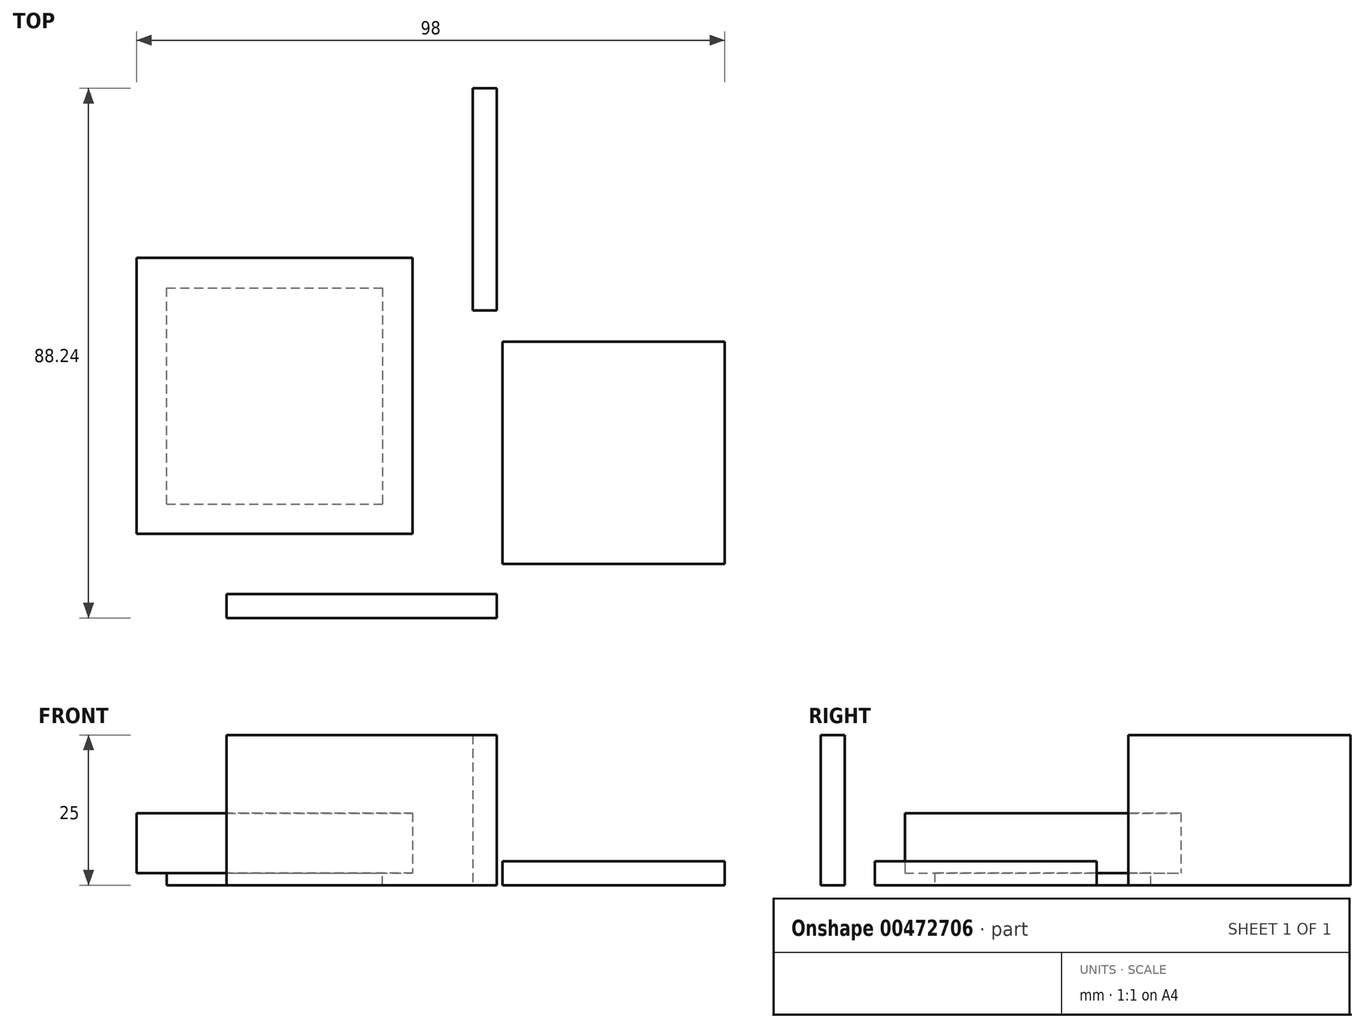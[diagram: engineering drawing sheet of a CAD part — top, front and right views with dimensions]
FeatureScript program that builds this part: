
annotation { "Feature Type Name" : "Feature", "Feature Type Description" : "" }
export const myFeature = defineFeature(function(context is Context, id is Id, definition is map)
    precondition{}
    {
        {
            var Q0;
            Q0=qCreatedBy(makeId("Top.planeOp"),FACE);
            var sketch = newSketch(context, id + "F0", { "sketchPlane" : qUnion([Q0])});
            skLineSegment(sketch, "E0", {"start": v(42, 5) * mm, "end": v(42, 42) * mm});
            skLineSegment(sketch, "E1", {"start": v(42, 42) * mm, "end": v(5, 42) * mm});
            skLineSegment(sketch, "E2", {"start": v(5, 42) * mm, "end": v(5, 5) * mm});
            skLineSegment(sketch, "E3", {"start": v(5, 5) * mm, "end": v(42, 5) * mm});
            skSolve(sketch);
        }
        {
            var Q0;
            Q0 = qSketchRegion(id + "F0", true);
            extrude(context, id + "F1", {"entities" : qUnion([Q0]), "depth" : 4 * mm});
        }
        {
            var Q0;
            Q0=qCreatedBy(makeId("Front.planeOp"),FACE);
            var sketch = newSketch(context, id + "F2", { "sketchPlane" : qUnion([Q0])});
            skLineSegment(sketch, "E4", {"start": v(0, 0) * mm, "end": v(4, 0) * mm});
            skLineSegment(sketch, "E5", {"start": v(4, 0) * mm, "end": v(4, 25) * mm});
            skLineSegment(sketch, "E6", {"start": v(4, 25) * mm, "end": v(-41, 25) * mm});
            skLineSegment(sketch, "E7", {"start": v(-41, 25) * mm, "end": v(-41, 0) * mm});
            skLineSegment(sketch, "E8", {"start": v(-41, 0) * mm, "end": v(0, 0) * mm});
            skSolve(sketch);
        }
        {
            var Q0;
            Q0 = qSketchRegion(id + "F2", true);
            extrude(context, id + "F3", {"entities" : qUnion([Q0]), "depth" : 4 * mm});
        }
        {
            var Q0;
            Q0=qCreatedBy(makeId("Right.planeOp"),FACE);
            var sketch = newSketch(context, id + "F4", { "sketchPlane" : qUnion([Q0])});
            skLineSegment(sketch, "E9", {"start": v(47.24, 0) * mm, "end": v(84.24, 0) * mm});
            skLineSegment(sketch, "E10", {"start": v(84.24, 0) * mm, "end": v(84.24, 25) * mm});
            skLineSegment(sketch, "E11", {"start": v(84.24, 25) * mm, "end": v(47.24, 25) * mm});
            skLineSegment(sketch, "E12", {"start": v(47.24, 25) * mm, "end": v(47.24, 0) * mm});
            skSolve(sketch);
        }
        {
            var Q0;
            Q0 = qSketchRegion(id + "F4", true);
            extrude(context, id + "F5", {"entities" : qUnion([Q0]), "depth" : 4 * mm});
        }
        {
            var Q0;
            Q0=qCreatedBy(makeId("Top.planeOp"),FACE);
            var sketch = newSketch(context, id + "F6", { "sketchPlane" : qUnion([Q0])});
            skLineSegment(sketch, "E13", {"start": v(0, 0) * mm, "end": v(0, 10) * mm, "construction": true});
            skLineSegment(sketch, "E14", {"start": v(0, 10) * mm, "end": v(-10, 10) * mm, "construction": true});
            skLineSegment(sketch, "E15", {"start": v(-10, 10) * mm, "end": v(-10, 56) * mm});
            skLineSegment(sketch, "E16", {"start": v(-10, 56) * mm, "end": v(-56, 56) * mm});
            skLineSegment(sketch, "E17", {"start": v(-56, 56) * mm, "end": v(-56, 10) * mm});
            skLineSegment(sketch, "E18", {"start": v(-56, 10) * mm, "end": v(-10, 10) * mm});
            skSolve(sketch);
        }
        {
            var Q0;
            Q0 = qSketchRegion(id + "F6", true);
            extrude(context, id + "F7", {"entities" : qUnion([Q0]), "depth" : 12 * mm});
        }
        {
            var Q0;
            Q0=qCreatedBy(makeId("Top.planeOp"),FACE);
            var sketch = newSketch(context, id + "F8", { "sketchPlane" : qUnion([Q0])});
            skLineSegment(sketch, "E19", {"start": v(0, 0) * mm, "end": v(0, 10) * mm, "construction": true});
            skLineSegment(sketch, "E20", {"start": v(0, 10) * mm, "end": v(-10, 10) * mm, "construction": true});
            skLineSegment(sketch, "E21", {"start": v(-10, 10) * mm, "end": v(-10, 56) * mm, "construction": true});
            skLineSegment(sketch, "E22", {"start": v(-10, 56) * mm, "end": v(-15, 56) * mm});
            skLineSegment(sketch, "E23", {"start": v(-15, 56) * mm, "end": v(-15, 15) * mm});
            skLineSegment(sketch, "E24", {"start": v(-15, 10) * mm, "end": v(-10, 10) * mm});
            skLineSegment(sketch, "E25", {"start": v(-10, 10) * mm, "end": v(-10, 56) * mm});
            skLineSegment(sketch, "E26", {"start": v(-10, 10) * mm, "end": v(-56, 10) * mm});
            skPoint(sketch, "E26.endSnap0", {"position": v(-12.5, 10) * mm});
            skLineSegment(sketch, "E27", {"start": v(-56, 10) * mm, "end": v(-56, 15) * mm});
            skLineSegment(sketch, "E28", {"start": v(-56, 15) * mm, "end": v(-15, 15) * mm});
            skSolve(sketch);
        }
        {
            var Q0;
            Q0 = qSketchRegion(id + "F8", true);
            extrude(context, id + "F9", {"entities" : qUnion([Q0]), "operationType" : NewBodyOperationType.REMOVE, "depth" : 2 * mm});
        }
        {
            var Q0;
            Q0=qCreatedBy(makeId("Top.planeOp"),FACE);
            var sketch = newSketch(context, id + "F10", { "sketchPlane" : qUnion([Q0])});
            skLineSegment(sketch, "E29", {"start": v(0, 0) * mm, "end": v(0, 10) * mm, "construction": true});
            skLineSegment(sketch, "E30", {"start": v(0, 10) * mm, "end": v(-10, 10) * mm, "construction": true});
            skLineSegment(sketch, "E31", {"start": v(-10, 10) * mm, "end": v(-10, 56) * mm, "construction": true});
            skLineSegment(sketch, "E32", {"start": v(-10, 56) * mm, "end": v(-56, 56) * mm});
            skLineSegment(sketch, "E33", {"start": v(-56, 56) * mm, "end": v(-56, 10) * mm});
            skLineSegment(sketch, "E34", {"start": v(-56, 10) * mm, "end": v(-51, 10) * mm});
            skLineSegment(sketch, "E35", {"start": v(-51, 10) * mm, "end": v(-51, 51) * mm});
            skLineSegment(sketch, "E36", {"start": v(-51, 51) * mm, "end": v(-10, 51) * mm});
            skLineSegment(sketch, "E37", {"start": v(-10, 51) * mm, "end": v(-10, 56) * mm});
            skSolve(sketch);
        }
        {
            var Q0;
            Q0 = qSketchRegion(id + "F10", true);
            extrude(context, id + "F11", {"entities" : qUnion([Q0]), "operationType" : NewBodyOperationType.REMOVE, "depth" : 2 * mm});
        }
    });
